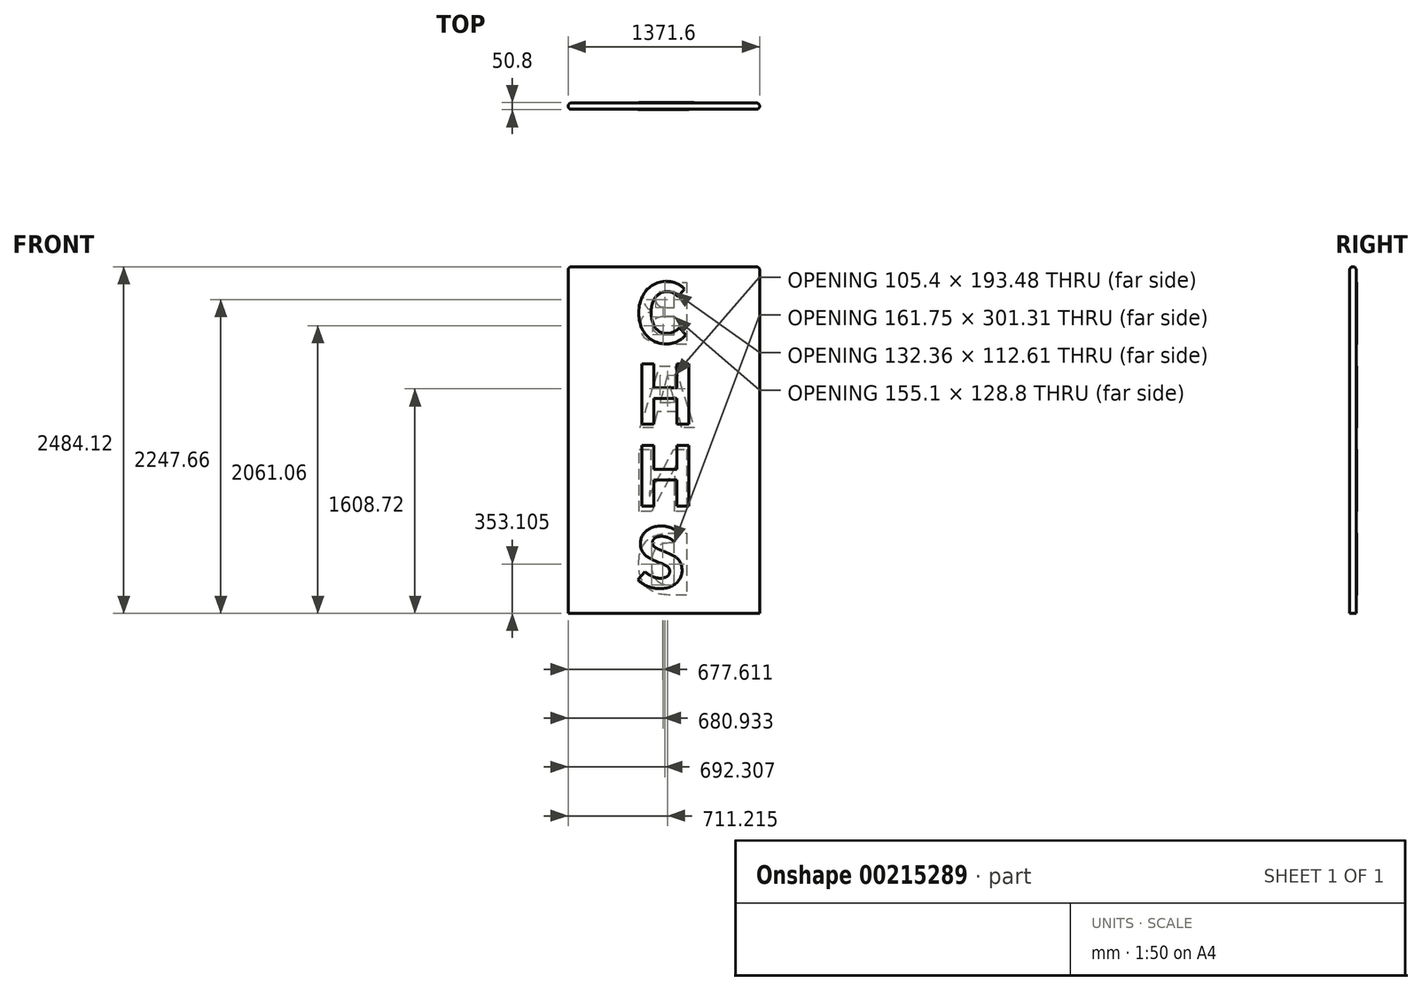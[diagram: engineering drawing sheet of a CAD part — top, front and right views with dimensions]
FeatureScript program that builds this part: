
annotation { "Feature Type Name" : "Feature", "Feature Type Description" : "" }
export const myFeature = defineFeature(function(context is Context, id is Id, definition is map)
    precondition{}
    {
        {
            var Q0;
            Q0=qCreatedBy(makeId("Front.planeOp"),FACE);
            var sketch = newSketch(context, id + "F0", { "sketchPlane" : qUnion([Q0])});
            skLineSegment(sketch, "E0.bottom", {"start": v(-685.8, 0) * mm, "end": v(685.8, 0) * mm});
            skLineSegment(sketch, "E0.top", {"start": v(-660.4, 2484.12) * mm, "end": v(660.4, 2484.12) * mm});
            skLineSegment(sketch, "E0.left", {"start": v(-685.8, 0) * mm, "end": v(-685.8, 2458.72) * mm});
            skLineSegment(sketch, "E0.right", {"start": v(685.8, 0) * mm, "end": v(685.8, 2458.72) * mm});
            skPoint(sketch, "E1.visualSharp", {"position": v(-685.8, 2484.12) * mm});
            skArc(sketch, "E1.filletArc", {"start": v(-660.4, 2484.12) * mm, "mid": v(-678.36, 2476.68) * mm, "end": v(-685.8, 2458.72) * mm});
            skPoint(sketch, "E2.visualSharp", {"position": v(685.8, 2484.12) * mm});
            skArc(sketch, "E2.filletArc", {"start": v(685.8, 2458.72) * mm, "mid": v(678.36, 2476.68) * mm, "end": v(660.4, 2484.12) * mm});
            skSolve(sketch);
        }
        {
            var Q0;
            Q0=makeQuery(id+"F0.imprint","IMPRINT",FACE,{"disambiguationData":[TD([[makeQuery(id+"F0.imprint","IMPRINT",EDGE,{"derivedFrom":sQuery(id+"F0.wireOp",EDGE,"E0.bottom")}),1.0]])]});
            extrude(context, id + "F1", {"entities" : qUnion([Q0]), "endBound" : BoundingType.SYMMETRIC, "depth" : 45.72 * mm});
        }
        {
            var Q0;
            Q0=makeQuery(id+"F1.opExtrude","CAP_EDGE",EDGE,{"disambiguationData":[OSD([sQuery(id+"F0.wireOp",EDGE,"E0.left")])],"isStart":false});
            var Q1;
            Q1=makeQuery(id+"F1.opExtrude","CAP_EDGE",EDGE,{"disambiguationData":[OSD([sQuery(id+"F0.wireOp",EDGE,"E0.left")])],"isStart":true});
            fillet(context, id + "F2", {"entities" : qUnion([Q0, Q1]), "radius" : 22.86 * mm, "tangentPropagation" : true, "allowEdgeOverflow" : false});
        }
        {
            var Q0;
            Q0=makeQuery(id+"F1.opExtrude","SWEPT_FACE",FACE,{"disambiguationData":[OSD([sQuery(id+"F0.wireOp",EDGE,"E0.bottom")])]});
            shell(context, id + "F3", {"entities" : qUnion([Q0]), "thickness" : 2.54 * mm});
        }
        {
            var Q0;
            Q0=makeQuery(id+"F1.opExtrude","CAP_FACE",FACE,{"disambiguationData":[OSD([sQuery(id+"F0.wireOp",EDGE,"E0.bottom"),sQuery(id+"F0.wireOp",EDGE,"E0.top"),sQuery(id+"F0.wireOp",EDGE,"E0.left"),sQuery(id+"F0.wireOp",EDGE,"E0.right"),sQuery(id+"F0.wireOp",EDGE,"E1.filletArc"),sQuery(id+"F0.wireOp",EDGE,"E2.filletArc")])],"isStart":false});
            var sketch = newSketch(context, id + "F4", { "sketchPlane" : qUnion([Q0])});
            skText(sketch, "E3", { "text": "C\nH\nH\nS", "fontName": "NotoSansCJKsc-Bold.otf"});
            const initialGuessF4  = {"E3": [-0.21124, 1.93874, 1, 0, 0.42092]};
            skSetInitialGuess(sketch, initialGuessF4);
            skSolve(sketch);
        }
        {
            var Q0;
            Q0 = qSketchRegion(id + "F4", true);
            extrude(context, id + "F5", {"entities" : qUnion([Q0]), "depth" : 2.54 * mm});
        }
        {
            var Q0;
            Q0=makeQuery(id+"F1.opExtrude","CAP_FACE",FACE,{"disambiguationData":[OSD([sQuery(id+"F0.wireOp",EDGE,"E0.bottom"),sQuery(id+"F0.wireOp",EDGE,"E0.top"),sQuery(id+"F0.wireOp",EDGE,"E0.left"),sQuery(id+"F0.wireOp",EDGE,"E0.right"),sQuery(id+"F0.wireOp",EDGE,"E1.filletArc"),sQuery(id+"F0.wireOp",EDGE,"E2.filletArc")])],"isStart":true});
            var sketch = newSketch(context, id + "F6", { "sketchPlane" : qUnion([Q0])});
            skText(sketch, "E4", { "text": "B\nA\nN\nD", "fontName": "NotoSansCJKsc-Bold.otf"});
            const initialGuessF6  = {"E4": [-0.2159, 1.92833, 1, 0, 0.43133]};
            skSetInitialGuess(sketch, initialGuessF6);
            skSolve(sketch);
        }
        {
            var Q0;
            Q0 = qSketchRegion(id + "F6", true);
            extrude(context, id + "F7", {"entities" : qUnion([Q0]), "depth" : 2.54 * mm});
        }
    });
